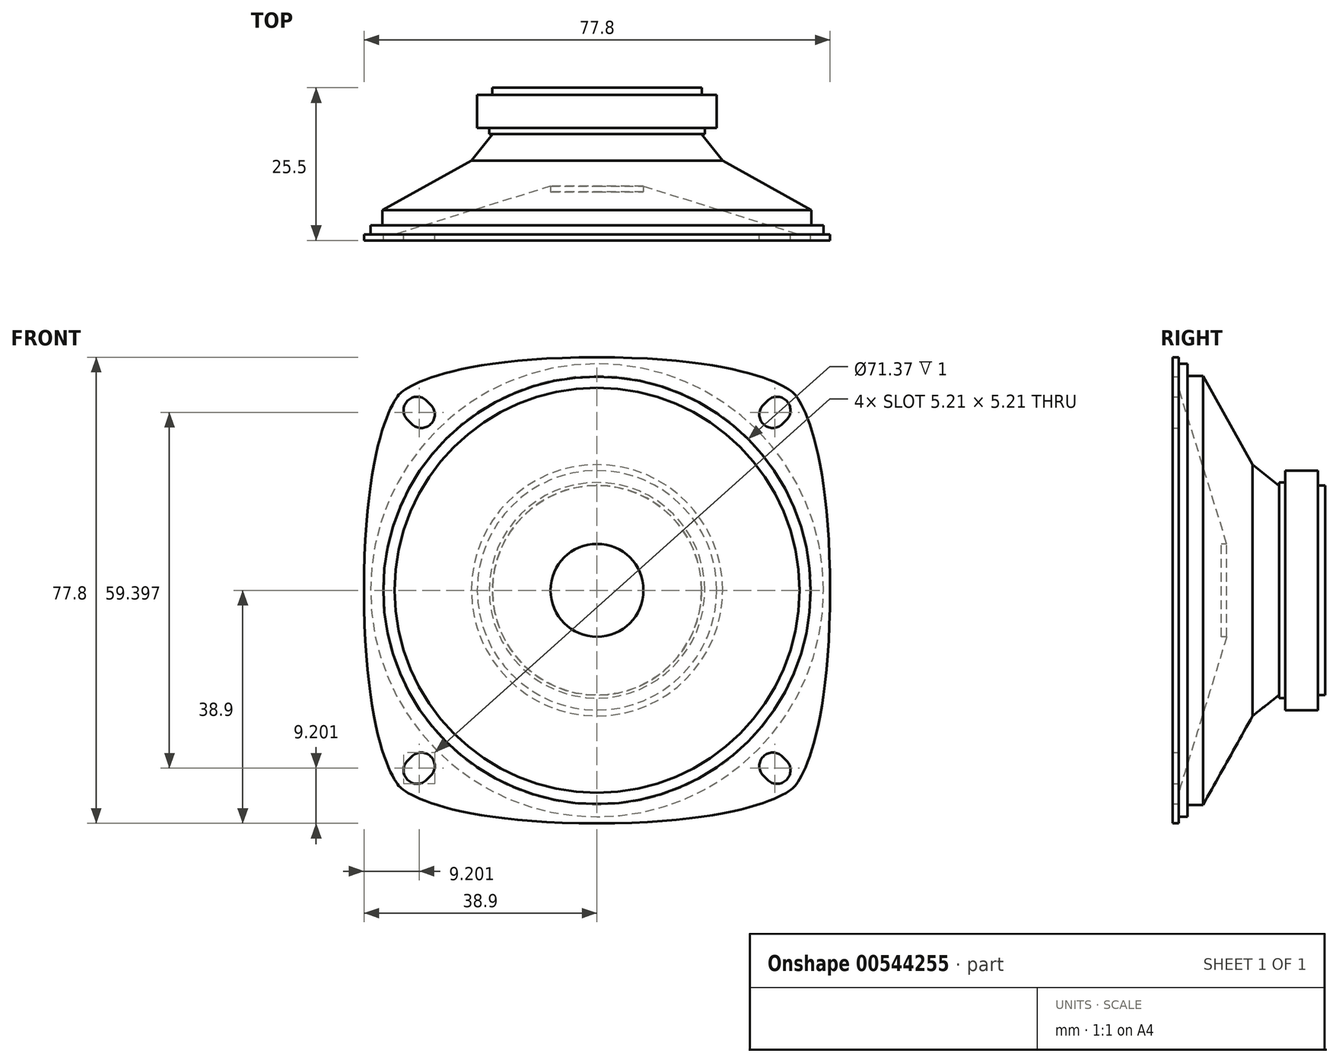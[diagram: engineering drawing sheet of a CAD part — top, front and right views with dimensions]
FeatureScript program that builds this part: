
annotation { "Feature Type Name" : "Feature", "Feature Type Description" : "" }
export const myFeature = defineFeature(function(context is Context, id is Id, definition is map)
    precondition{}
    {
        {
            var Q0;
            Q0=qCreatedBy(makeId("Front.planeOp"),FACE);
            var sketch = newSketch(context, id + "F0", { "sketchPlane" : qUnion([Q0])});
            skCircle(sketch, "E0", {"center": v(0, 0) * mm, "radius": 35.68 * mm, "construction": true});
            skLineSegment(sketch, "E1.bottom", {"start": v(38.9, -38.9) * mm, "end": v(-38.9, -38.9) * mm, "construction": true});
            skLineSegment(sketch, "E1.top", {"start": v(38.9, 38.9) * mm, "end": v(-38.9, 38.9) * mm, "construction": true});
            skLineSegment(sketch, "E1.left", {"start": v(38.9, -38.9) * mm, "end": v(38.9, 38.9) * mm, "construction": true});
            skLineSegment(sketch, "E1.right", {"start": v(-38.9, -38.9) * mm, "end": v(-38.9, 38.9) * mm, "construction": true});
            skLineSegment(sketch, "E2", {"start": v(0, 0) * mm, "end": v(-29.34, 29.34) * mm, "construction": true});
            skLineSegment(sketch, "E3", {"start": v(-29.34, 29.34) * mm, "end": v(-30.05, 30.05) * mm, "construction": true});
            skLineSegment(sketch, "E4", {"start": v(-30.05, 30.05) * mm, "end": v(-38.9, 38.9) * mm, "construction": true});
            skArc(sketch, "E5.0.startCap", {"start": v(-27.75, 30.94) * mm, "mid": v(-27.75, 27.75) * mm, "end": v(-30.94, 27.75) * mm});
            skArc(sketch, "E5.0.endCap", {"start": v(-31.64, 28.46) * mm, "mid": v(-31.64, 31.64) * mm, "end": v(-28.46, 31.64) * mm});
            skLineSegment(sketch, "E5.0.left", {"start": v(-30.94, 27.75) * mm, "end": v(-31.64, 28.46) * mm});
            skLineSegment(sketch, "E5.0.right", {"start": v(-27.75, 30.94) * mm, "end": v(-28.46, 31.64) * mm});
            skPoint(sketch, "E6", {"position": v(-29.7, 29.7) * mm});
            skLineSegment(sketch, "E7", {"start": v(-25.23, -25.23) * mm, "end": v(25.23, 25.23) * mm, "construction": true});
            skLineSegment(sketch, "E8", {"start": v(25.23, 25.23) * mm, "end": v(32.88, 32.88) * mm, "construction": true});
            skLineSegment(sketch, "E9", {"start": v(-25.23, -25.23) * mm, "end": v(-32.88, -32.88) * mm, "construction": true});
            skLineSegment(sketch, "E10", {"start": v(26.86, 38.9) * mm, "end": v(38.9, 26.86) * mm, "construction": true});
            skFitSpline(sketch, "E11", {"points": [v(32.88, 32.88) * mm, v(0, 38.9) * mm], "startDerivative": vector(-15.4, 15.4) * mm, "endDerivative": vector(-77.58, 0) * mm, "construction": true});
            skSolve(sketch);
        }
        {
            var Q0;
            Q0=qCreatedBy(makeId("Front.planeOp"),FACE);
            var sketch = newSketch(context, id + "F1", { "sketchPlane" : qUnion([Q0])});
            skArc(sketch, "E12.0.0", {"start": v(-28.46, 31.64) * mm, "mid": v(-31.64, 31.64) * mm, "end": v(-31.64, 28.46) * mm});
            skLineSegment(sketch, "E12.0.1", {"start": v(-31.64, 28.46) * mm, "end": v(-30.94, 27.75) * mm});
            skArc(sketch, "E12.0.2", {"start": v(-30.94, 27.75) * mm, "mid": v(-27.75, 27.75) * mm, "end": v(-27.75, 30.94) * mm});
            skLineSegment(sketch, "E12.0.3", {"start": v(-27.75, 30.94) * mm, "end": v(-28.46, 31.64) * mm});
            skCircle(sketch, "E13.1", {"center": v(0, 0) * mm, "radius": 35.68 * mm});
            skArc(sketch, "E14.MirrorCS", {"start": v(28.46, 31.64) * mm, "mid": v(31.64, 31.64) * mm, "end": v(31.64, 28.46) * mm});
            skLineSegment(sketch, "E15.MirrorCS", {"start": v(27.75, 30.94) * mm, "end": v(28.46, 31.64) * mm});
            skLineSegment(sketch, "E16.MirrorCS", {"start": v(31.64, 28.46) * mm, "end": v(30.94, 27.75) * mm});
            skArc(sketch, "E17.MirrorCS", {"start": v(30.94, 27.75) * mm, "mid": v(27.75, 27.75) * mm, "end": v(27.75, 30.94) * mm});
            skArc(sketch, "E18.MirrorCS", {"start": v(30.94, -27.75) * mm, "mid": v(27.75, -27.75) * mm, "end": v(27.75, -30.94) * mm});
            skLineSegment(sketch, "E19.MirrorCS", {"start": v(31.64, -28.46) * mm, "end": v(30.94, -27.75) * mm});
            skLineSegment(sketch, "E20.MirrorCS", {"start": v(27.75, -30.94) * mm, "end": v(28.46, -31.64) * mm});
            skArc(sketch, "E21.MirrorCS", {"start": v(28.46, -31.64) * mm, "mid": v(31.64, -31.64) * mm, "end": v(31.64, -28.46) * mm});
            skLineSegment(sketch, "E22.MirrorCS", {"start": v(-31.64, -28.46) * mm, "end": v(-30.94, -27.75) * mm});
            skLineSegment(sketch, "E23.MirrorCS", {"start": v(-27.75, -30.94) * mm, "end": v(-28.46, -31.64) * mm});
            skArc(sketch, "E24.MirrorCS", {"start": v(-30.94, -27.75) * mm, "mid": v(-27.75, -27.75) * mm, "end": v(-27.75, -30.94) * mm});
            skArc(sketch, "E25.MirrorCS", {"start": v(-28.46, -31.64) * mm, "mid": v(-31.64, -31.64) * mm, "end": v(-31.64, -28.46) * mm});
            skFitSpline(sketch, "E26", {"points": [v(32.88, 32.88) * mm, v(0, 38.9) * mm], "startDerivative": vector(-4.08, 4.08) * mm, "endDerivative": vector(-70.58, 0) * mm});
            skFitSpline(sketch, "E27.MirrorCS", {"points": [v(32.88, 32.88) * mm, v(38.9, 0) * mm], "startDerivative": vector(4.08, -4.08) * mm, "endDerivative": vector(0, -70.58) * mm});
            skFitSpline(sketch, "E28.MirrorCS", {"points": [v(-32.88, 32.88) * mm, v(-38.9, 0) * mm], "startDerivative": vector(-4.08, -4.08) * mm, "endDerivative": vector(0, -70.58) * mm});
            skFitSpline(sketch, "E29.MirrorCS", {"points": [v(-32.88, 32.88) * mm, v(0, 38.9) * mm], "startDerivative": vector(4.08, 4.08) * mm, "endDerivative": vector(70.58, 0) * mm});
            skFitSpline(sketch, "E30.MirrorCS", {"points": [v(32.88, -32.88) * mm, v(38.9, 0) * mm], "startDerivative": vector(4.08, 4.08) * mm, "endDerivative": vector(0, 70.58) * mm});
            skFitSpline(sketch, "E31.MirrorCS", {"points": [v(32.88, -32.88) * mm, v(0, -38.9) * mm], "startDerivative": vector(-4.08, -4.08) * mm, "endDerivative": vector(-70.58, 0) * mm});
            skFitSpline(sketch, "E32.MirrorCS", {"points": [v(-32.88, -32.88) * mm, v(0, -38.9) * mm], "startDerivative": vector(4.08, -4.08) * mm, "endDerivative": vector(70.58, 0) * mm});
            skFitSpline(sketch, "E33.MirrorCS", {"points": [v(-32.88, -32.88) * mm, v(-38.9, 0) * mm], "startDerivative": vector(-4.08, 4.08) * mm, "endDerivative": vector(0, 70.58) * mm});
            skSolve(sketch);
        }
        {
            var Q0;
            Q0 = qSketchRegion(id + "F1", true);
            extrude(context, id + "F2", {"entities" : qUnion([Q0]), "depth" : 1 * mm, "offsetDistance" : 25 * mm});
        }
        {
            var Q0;
            Q0=qCreatedBy(makeId("Right.planeOp"),FACE);
            var sketch = newSketch(context, id + "F3", { "sketchPlane" : qUnion([Q0])});
            skLineSegment(sketch, "E34", {"start": v(4.1, -35.81) * mm, "end": v(12.36, -20.99) * mm});
            skLineSegment(sketch, "E35", {"start": v(12.36, -20.99) * mm, "end": v(16.8, -17.46) * mm});
            skLineSegment(sketch, "E36", {"start": v(16.8, -17.46) * mm, "end": v(16.8, -18) * mm});
            skLineSegment(sketch, "E37", {"start": v(16.8, -18) * mm, "end": v(17.8, -18) * mm});
            skLineSegment(sketch, "E38", {"start": v(17.8, -18) * mm, "end": v(17.8, -20) * mm});
            skLineSegment(sketch, "E39", {"start": v(17.8, -20) * mm, "end": v(23.3, -20) * mm});
            skLineSegment(sketch, "E40", {"start": v(23.3, -20) * mm, "end": v(23.3, -17.5) * mm});
            skLineSegment(sketch, "E41", {"start": v(23.3, -17.5) * mm, "end": v(24.5, -17.5) * mm});
            skLineSegment(sketch, "E42", {"start": v(24.5, -17.5) * mm, "end": v(24.5, 0) * mm});
            skLineSegment(sketch, "E43", {"start": v(24.5, 0) * mm, "end": v(7.13, 0) * mm});
            skLineSegment(sketch, "E44", {"start": v(7.13, 0) * mm, "end": v(7.13, -7.75) * mm});
            skLineSegment(sketch, "E45", {"start": v(7.13, -7.75) * mm, "end": v(8.06, -7.75) * mm});
            skLineSegment(sketch, "E46", {"start": v(8.06, -7.75) * mm, "end": v(0, -33.81) * mm});
            skLineSegment(sketch, "E47", {"start": v(0, -33.81) * mm, "end": v(0, -37.81) * mm});
            skLineSegment(sketch, "E48", {"start": v(0, 0) * mm, "end": v(36.1, 0) * mm, "construction": true});
            skLineSegment(sketch, "E49", {"start": v(14.58, -19.22) * mm, "end": v(14.58, -49.46) * mm, "construction": true});
            skLineSegment(sketch, "E50", {"start": v(0, -37.81) * mm, "end": v(1.5, -37.81) * mm});
            skLineSegment(sketch, "E51", {"start": v(1.5, -37.81) * mm, "end": v(1.5, -35.81) * mm});
            skLineSegment(sketch, "E52", {"start": v(1.5, -35.81) * mm, "end": v(4.1, -35.81) * mm});
            skSolve(sketch);
        }
        {
            var Q0;
            Q0 = qSketchRegion(id + "F3", true);
            var Q1;
            Q1=sQuery(id+"F3.wireOp",EDGE,"E48");
            revolve(context, id + "F4", {"operationType" : NewBodyOperationType.ADD, "entities" : qUnion([Q0]), "axis" : qUnion([Q1]), "revolveType" : RevolveType.FULL});
        }
    });
